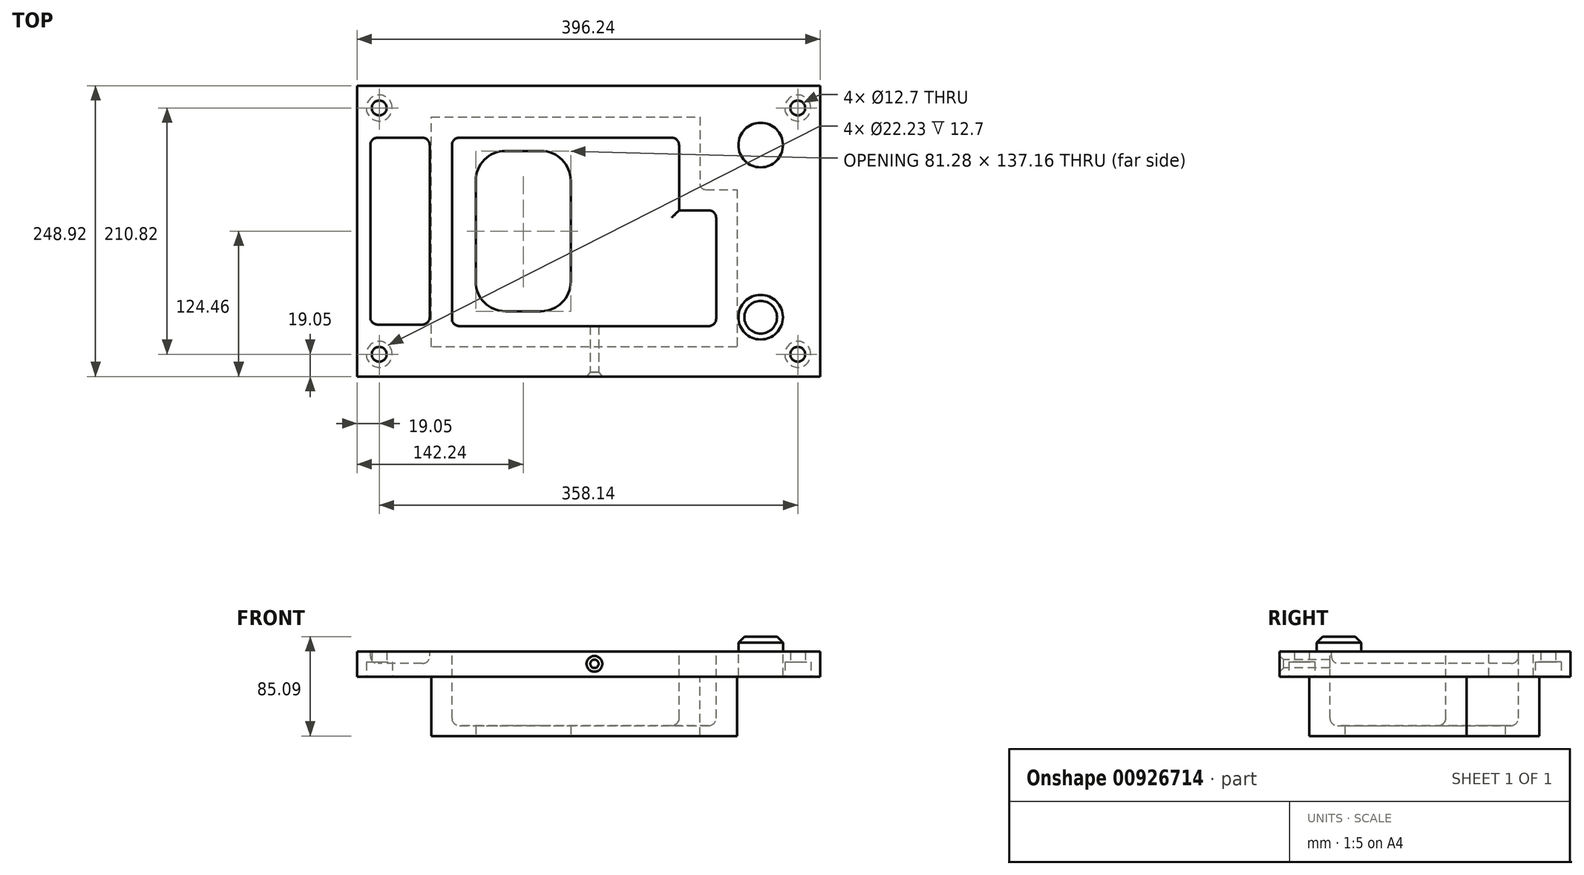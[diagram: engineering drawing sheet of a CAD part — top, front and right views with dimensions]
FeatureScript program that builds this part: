
annotation { "Feature Type Name" : "Feature", "Feature Type Description" : "" }
export const myFeature = defineFeature(function(context is Context, id is Id, definition is map)
    precondition{}
    {
        {
            var Q0;
            Q0=qCreatedBy(makeId("Top.planeOp"),FACE);
            var sketch = newSketch(context, id + "F0", { "sketchPlane" : qUnion([Q0])});
            skLineSegment(sketch, "E0.bottom", {"start": v(198.12, 124.46) * mm, "end": v(-198.12, 124.46) * mm});
            skLineSegment(sketch, "E0.top", {"start": v(198.12, -124.46) * mm, "end": v(-198.12, -124.46) * mm});
            skLineSegment(sketch, "E0.left", {"start": v(198.12, 124.46) * mm, "end": v(198.12, -124.46) * mm});
            skLineSegment(sketch, "E0.right", {"start": v(-198.12, 124.46) * mm, "end": v(-198.12, -124.46) * mm});
            skPoint(sketch, "E0.middle", {"position": v(0, 0) * mm});
            skSolve(sketch);
        }
        {
            var Q0;
            Q0=qSketchRegion(id+"F0",true);
            extrude(context, id + "F1", {"entities" : qUnion([Q0]), "oppositeDirection" : true, "depth" : 21.59 * mm, "offsetDistance" : 25.4 * mm});
        }
        {
            var Q0;
            Q0=makeQuery(id+"F1.opExtrude","CAP_FACE",FACE,{"disambiguationData":[OSD([sQuery(id+"F0.wireOp",EDGE,"E0.bottom"),sQuery(id+"F0.wireOp",EDGE,"E0.top"),sQuery(id+"F0.wireOp",EDGE,"E0.left"),sQuery(id+"F0.wireOp",EDGE,"E0.right")])],"isStart":false});
            var sketch = newSketch(context, id + "F2", { "sketchPlane" : qUnion([Q0])});
            skLineSegment(sketch, "E1", {"start": v(-134.62, 99.06) * mm, "end": v(-134.62, -97.79) * mm});
            skLineSegment(sketch, "E2", {"start": v(-134.62, -97.79) * mm, "end": v(95.25, -97.79) * mm});
            skLineSegment(sketch, "E3", {"start": v(95.25, -97.8) * mm, "end": v(95.25, -35.56) * mm});
            skLineSegment(sketch, "E4", {"start": v(95.25, -35.56) * mm, "end": v(127, -35.56) * mm});
            skLineSegment(sketch, "E5", {"start": v(127, -35.56) * mm, "end": v(127, 99.06) * mm});
            skLineSegment(sketch, "E6", {"start": v(127, 99.06) * mm, "end": v(-134.62, 99.06) * mm});
            skSolve(sketch);
        }
        {
            var Q0;
            Q0=qSketchRegion(id+"F2",true);
            extrude(context, id + "F3", {"entities" : qUnion([Q0]), "operationType" : NewBodyOperationType.ADD, "depth" : 50.8 * mm, "offsetDistance" : 25.4 * mm});
        }
        {
            var Q0;
            Q0=makeQuery(id+"F1.opExtrude","CAP_FACE",FACE,{"disambiguationData":[OSD([sQuery(id+"F0.wireOp",EDGE,"E0.bottom"),sQuery(id+"F0.wireOp",EDGE,"E0.top"),sQuery(id+"F0.wireOp",EDGE,"E0.left"),sQuery(id+"F0.wireOp",EDGE,"E0.right")])],"isStart":true});
            var sketch = newSketch(context, id + "F4", { "sketchPlane" : qUnion([Q0])});
            skLineSegment(sketch, "E7.0", {"start": v(127, -99.06) * mm, "end": v(-134.62, -99.06) * mm, "construction": true});
            skLineSegment(sketch, "E8.0", {"start": v(127, 35.56) * mm, "end": v(127, -99.06) * mm, "construction": true});
            skPoint(sketch, "E9.0", {"position": v(111.12, 35.56) * mm});
            skLineSegment(sketch, "E10.0", {"start": v(95.25, 97.8) * mm, "end": v(95.25, 35.56) * mm, "construction": true});
            skLineSegment(sketch, "E11.0", {"start": v(95.25, 35.56) * mm, "end": v(127, 35.56) * mm, "construction": true});
            skLineSegment(sketch, "E12.0", {"start": v(-134.62, 97.79) * mm, "end": v(95.25, 97.79) * mm, "construction": true});
            skLineSegment(sketch, "E13.0", {"start": v(-134.62, -99.06) * mm, "end": v(-134.62, 97.79) * mm, "construction": true});
            skLineSegment(sketch, "E14", {"start": v(109.22, -81.28) * mm, "end": v(109.22, 17.78) * mm});
            skLineSegment(sketch, "E15", {"start": v(109.22, 17.78) * mm, "end": v(77.47, 17.78) * mm});
            skLineSegment(sketch, "E16", {"start": v(77.47, 17.78) * mm, "end": v(77.47, 80) * mm});
            skLineSegment(sketch, "E17", {"start": v(77.47, 80) * mm, "end": v(-116.84, 80) * mm});
            skLineSegment(sketch, "E18", {"start": v(-116.84, 80) * mm, "end": v(-116.84, -81.28) * mm});
            skLineSegment(sketch, "E19", {"start": v(-116.84, -81.28) * mm, "end": v(109.22, -81.28) * mm});
            skSolve(sketch);
        }
        {
            var Q0;
            Q0=qSketchRegion(id+"F4",true);
            extrude(context, id + "F5", {"entities" : qUnion([Q0]), "operationType" : NewBodyOperationType.REMOVE, "oppositeDirection" : true, "depth" : 63.5 * mm, "offsetDistance" : 25.4 * mm});
        }
        {
            var Q0;
            Q0=makeQuery(id+"F5.boolean.opBoolean","COPY",FACE,{"derivedFrom":makeQuery(id+"F5.opExtrude","CAP_FACE",FACE,{"disambiguationData":[OSD([sQuery(id+"F4.wireOp",EDGE,"E14"),sQuery(id+"F4.wireOp",EDGE,"E15"),sQuery(id+"F4.wireOp",EDGE,"E16"),sQuery(id+"F4.wireOp",EDGE,"E17"),sQuery(id+"F4.wireOp",EDGE,"E18"),sQuery(id+"F4.wireOp",EDGE,"E19")])],"isStart":false})});
            var Q1;
            Q1=makeQuery(id+"F5.boolean.opBoolean","COPY",EDGE,{"derivedFrom":makeQuery(id+"F5.opExtrude","SWEPT_EDGE",EDGE,{"disambiguationData":[OSD([sQuery(id+"F4.wireOp",EDGE,"E14"),sQuery(id+"F4.wireOp",EDGE,"E19")])]})});
            var Q2;
            Q2=makeQuery(id+"F5.boolean.opBoolean","COPY",EDGE,{"derivedFrom":makeQuery(id+"F5.opExtrude","SWEPT_EDGE",EDGE,{"disambiguationData":[OSD([sQuery(id+"F4.wireOp",EDGE,"E18"),sQuery(id+"F4.wireOp",EDGE,"E19")])]})});
            var Q3;
            Q3=makeQuery(id+"F5.boolean.opBoolean","COPY",EDGE,{"derivedFrom":makeQuery(id+"F5.opExtrude","SWEPT_EDGE",EDGE,{"disambiguationData":[OSD([sQuery(id+"F4.wireOp",EDGE,"E17"),sQuery(id+"F4.wireOp",EDGE,"E18")])]})});
            var Q4;
            Q4=makeQuery(id+"F5.boolean.opBoolean","COPY",EDGE,{"derivedFrom":makeQuery(id+"F5.opExtrude","SWEPT_EDGE",EDGE,{"disambiguationData":[OSD([sQuery(id+"F4.wireOp",EDGE,"E14"),sQuery(id+"F4.wireOp",EDGE,"E15")])]})});
            var Q5;
            Q5=makeQuery(id+"F5.boolean.opBoolean","COPY",EDGE,{"derivedFrom":makeQuery(id+"F5.opExtrude","SWEPT_EDGE",EDGE,{"disambiguationData":[OSD([sQuery(id+"F4.wireOp",EDGE,"E16"),sQuery(id+"F4.wireOp",EDGE,"E17")])]})});
            fillet(context, id + "F6", {"entities" : qUnion([Q0, Q1, Q2, Q3, Q4, Q5]), "radius" : 6.35 * mm, "tangentPropagation" : true, "allowEdgeOverflow" : false});
        }
        {
            var Q0;
            Q0=makeQuery(id+"F3.opExtrude","SWEPT_EDGE",EDGE,{"disambiguationData":[OSD([sQuery(id+"F2.wireOp",EDGE,"E3"),sQuery(id+"F2.wireOp",EDGE,"E4")])]});
            fillet(context, id + "F7", {"entities" : qUnion([Q0]), "radius" : 5.08 * mm, "tangentPropagation" : true, "allowEdgeOverflow" : false});
        }
        {
            var Q0;
            Q0=makeQuery(id+"F3.opExtrude","CAP_FACE",FACE,{"disambiguationData":[OSD([sQuery(id+"F2.wireOp",EDGE,"E1"),sQuery(id+"F2.wireOp",EDGE,"E2"),sQuery(id+"F2.wireOp",EDGE,"E3"),sQuery(id+"F2.wireOp",EDGE,"E4"),sQuery(id+"F2.wireOp",EDGE,"E5"),sQuery(id+"F2.wireOp",EDGE,"E6")])],"isStart":false});
            var sketch = newSketch(context, id + "F8", { "sketchPlane" : qUnion([Q0])});
            skLineSegment(sketch, "E20.bottom", {"start": v(-96.52, -68.58) * mm, "end": v(-15.24, -68.58) * mm});
            skLineSegment(sketch, "E20.top", {"start": v(-96.52, 68.58) * mm, "end": v(-15.24, 68.58) * mm});
            skLineSegment(sketch, "E20.left", {"start": v(-96.52, -68.58) * mm, "end": v(-96.52, 68.58) * mm});
            skLineSegment(sketch, "E20.right", {"start": v(-15.24, -68.58) * mm, "end": v(-15.24, 68.58) * mm});
            skPoint(sketch, "E20.middle", {"position": v(-55.88, 0) * mm});
            skSolve(sketch);
        }
        {
            var Q0;
            Q0=qSketchRegion(id+"F8",true);
            extrude(context, id + "F9", {"entities" : qUnion([Q0]), "operationType" : NewBodyOperationType.REMOVE, "endBound" : BoundingType.THROUGH_ALL, "oppositeDirection" : true, "depth" : 25.4 * mm, "offsetDistance" : 25.4 * mm});
        }
        {
            var Q0;
            Q0=makeQuery(id+"F1.opExtrude","CAP_FACE",FACE,{"disambiguationData":[OSD([sQuery(id+"F0.wireOp",EDGE,"E0.bottom"),sQuery(id+"F0.wireOp",EDGE,"E0.top"),sQuery(id+"F0.wireOp",EDGE,"E0.left"),sQuery(id+"F0.wireOp",EDGE,"E0.right")])],"isStart":true});
            var sketch = newSketch(context, id + "F10", { "sketchPlane" : qUnion([Q0])});
            skLineSegment(sketch, "E21.bottom", {"start": v(-135.9, 80) * mm, "end": v(-186.7, 80) * mm});
            skLineSegment(sketch, "E21.top", {"start": v(-135.9, -80) * mm, "end": v(-186.7, -80) * mm});
            skLineSegment(sketch, "E21.left", {"start": v(-135.9, 80) * mm, "end": v(-135.9, -80) * mm});
            skLineSegment(sketch, "E21.right", {"start": v(-186.7, 80) * mm, "end": v(-186.7, -80) * mm});
            skPoint(sketch, "E21.middle", {"position": v(-161.3, 0) * mm});
            skSolve(sketch);
        }
        {
            var Q0;
            Q0=qSketchRegion(id+"F10",true);
            extrude(context, id + "F11", {"entities" : qUnion([Q0]), "operationType" : NewBodyOperationType.REMOVE, "oppositeDirection" : true, "depth" : 10.4 * mm, "offsetDistance" : 25.4 * mm});
        }
        {
            var Q0;
            Q0=makeQuery(id+"F11.boolean.opBoolean","COPY",FACE,{"derivedFrom":makeQuery(id+"F11.opExtrude","CAP_FACE",FACE,{"disambiguationData":[OSD([sQuery(id+"F10.wireOp",EDGE,"E21.bottom"),sQuery(id+"F10.wireOp",EDGE,"E21.top"),sQuery(id+"F10.wireOp",EDGE,"E21.left"),sQuery(id+"F10.wireOp",EDGE,"E21.right")])],"isStart":false})});
            var Q1;
            Q1=makeQuery(id+"F11.boolean.opBoolean","COPY",EDGE,{"derivedFrom":makeQuery(id+"F11.opExtrude","SWEPT_EDGE",EDGE,{"disambiguationData":[OSD([sQuery(id+"F10.wireOp",EDGE,"E21.bottom"),sQuery(id+"F10.wireOp",EDGE,"E21.right")])]})});
            var Q2;
            Q2=makeQuery(id+"F11.boolean.opBoolean","COPY",EDGE,{"derivedFrom":makeQuery(id+"F11.opExtrude","SWEPT_EDGE",EDGE,{"disambiguationData":[OSD([sQuery(id+"F10.wireOp",EDGE,"E21.bottom"),sQuery(id+"F10.wireOp",EDGE,"E21.left")])]})});
            var Q3;
            Q3=makeQuery(id+"F11.boolean.opBoolean","COPY",EDGE,{"derivedFrom":makeQuery(id+"F11.opExtrude","SWEPT_EDGE",EDGE,{"disambiguationData":[OSD([sQuery(id+"F10.wireOp",EDGE,"E21.top"),sQuery(id+"F10.wireOp",EDGE,"E21.left")])]})});
            var Q4;
            Q4=makeQuery(id+"F11.boolean.opBoolean","COPY",EDGE,{"derivedFrom":makeQuery(id+"F11.opExtrude","SWEPT_EDGE",EDGE,{"disambiguationData":[OSD([sQuery(id+"F10.wireOp",EDGE,"E21.top"),sQuery(id+"F10.wireOp",EDGE,"E21.right")])]})});
            fillet(context, id + "F12", {"entities" : qUnion([Q0, Q1, Q2, Q3, Q4]), "radius" : 6.35 * mm, "tangentPropagation" : true, "allowEdgeOverflow" : false});
        }
        {
            var Q0;
            Q0=makeQuery(id+"F1.opExtrude","CAP_FACE",FACE,{"disambiguationData":[OSD([sQuery(id+"F0.wireOp",EDGE,"E0.bottom"),sQuery(id+"F0.wireOp",EDGE,"E0.top"),sQuery(id+"F0.wireOp",EDGE,"E0.left"),sQuery(id+"F0.wireOp",EDGE,"E0.right")])],"isStart":true});
            var sketch = newSketch(context, id + "F13", { "sketchPlane" : qUnion([Q0])});
            skLineSegment(sketch, "E22.bottom", {"start": v(160.02, 86.36) * mm, "end": v(134.62, 86.36) * mm});
            skLineSegment(sketch, "E22.top", {"start": v(160.02, 60.96) * mm, "end": v(134.62, 60.96) * mm});
            skLineSegment(sketch, "E22.left", {"start": v(160.02, 86.36) * mm, "end": v(160.02, 60.96) * mm});
            skLineSegment(sketch, "E22.right", {"start": v(134.62, 86.36) * mm, "end": v(134.62, 60.96) * mm});
            skPoint(sketch, "E22.middle", {"position": v(147.32, 73.66) * mm});
            skCircle(sketch, "E23", {"center": v(147.32, -73.66) * mm, "radius": 19.05 * mm});
            skSolve(sketch);
        }
        {
            var Q0;
            Q0=makeQuery(id+"F13.imprint","IMPRINT",FACE,{"disambiguationData":[TD([[makeQuery(id+"F13.imprint","IMPRINT",EDGE,{"derivedFrom":sQuery(id+"F13.wireOp",EDGE,"E23")}),1.0]])]});
            extrude(context, id + "F14", {"entities" : qUnion([Q0]), "operationType" : NewBodyOperationType.ADD, "depth" : 12.7 * mm, "offsetDistance" : 25.4 * mm});
        }
        {
            var Q0;
            Q0=makeQuery(id+"F14.opExtrude","CAP_FACE",FACE,{"disambiguationData":[OSD([sQuery(id+"F13.wireOp",EDGE,"E22.bottom"),sQuery(id+"F13.wireOp",EDGE,"E22.top"),sQuery(id+"F13.wireOp",EDGE,"E22.left"),sQuery(id+"F13.wireOp",EDGE,"E22.right")])],"isStart":false});
            var Q1;
            Q1=makeQuery(id+"F14.opExtrude","CAP_FACE",FACE,{"disambiguationData":[OSD([sQuery(id+"F13.wireOp",EDGE,"E23")])],"isStart":false});
            chamfer(context, id + "F15", {"entities" : qUnion([Q0, Q1]), "width" : 5.08 * mm, "tangentPropagation" : true});
        }
        {
            var Q0;
            Q0=makeQuery(id+"F1.opExtrude","SWEPT_FACE",FACE,{"disambiguationData":[OSD([sQuery(id+"F0.wireOp",EDGE,"E0.top")])]});
            var sketch = newSketch(context, id + "F16", { "sketchPlane" : qUnion([Q0])});
            skPoint(sketch, "E24", {"position": v(5.08, -10.67) * mm});
            skSolve(sketch);
        }
        {
            var Q0;
            Q0=sQuery(id+"F16.wireOp",VERTEX,"E24");
            var Q1;
            Q1=makeQuery(id+"F1.opExtrude","SWEPT_BODY",BODY,{"disambiguationData":[OSD([sQuery(id+"F0.wireOp",EDGE,"E0.bottom"),sQuery(id+"F0.wireOp",EDGE,"E0.top"),sQuery(id+"F0.wireOp",EDGE,"E0.left"),sQuery(id+"F0.wireOp",EDGE,"E0.right")])]});
            hole(context, id + "F17", {"style" : HoleStyle.C_SINK, "endStyle" : HoleEndStyle.BLIND, "standardTappedOrClearance" : lookupTablePath({ "fit" : "Normal (ASME)", "standard" : "ANSI", "size" : "1/4", "type" : "Clearance" }), "standardBlindInLast" : lookupTablePath({ "fit" : "Normal", "standard" : "ANSI", "size" : "1/4", "type" : "Clearance" }), "holeDiameter" : 7.14 * mm, "cSinkDiameter" : 13.5 * mm, "cSinkAngle" : 82 * degree, "majorDiameter" : 6.35 * mm, "holeDepth" : 127 * mm, "isTappedThrough" : true, "tappedDepth" : 12.7 * mm, "tapClearance" : 3, "locations" : qUnion([Q0]), "scope" : qUnion([Q1])});
        }
        {
            var Q0;
            Q0=makeQuery(id+"F2.imprint","IMPRINT",FACE,{"disambiguationData":[TD([[makeQuery(id+"F2.imprint","IMPRINT",EDGE,{"derivedFrom":sQuery(id+"F2.wireOp",EDGE,"E1")}),-1.0]])]});
            var sketch = newSketch(context, id + "F18", { "sketchPlane" : qUnion([Q0])});
            skLineSegment(sketch, "E25.bottom", {"start": v(179.07, -105.41) * mm, "end": v(-179.07, -105.41) * mm});
            skLineSegment(sketch, "E25.top", {"start": v(179.07, 105.41) * mm, "end": v(-179.07, 105.41) * mm});
            skLineSegment(sketch, "E25.left", {"start": v(179.07, -105.41) * mm, "end": v(179.07, 105.41) * mm});
            skLineSegment(sketch, "E25.right", {"start": v(-179.07, -105.41) * mm, "end": v(-179.07, 105.41) * mm});
            skPoint(sketch, "E25.middle", {"position": v(0, 0) * mm});
            skSolve(sketch);
        }
        {
            var Q0;
            Q0=sQuery(id+"F18.wireOp",VERTEX,"E25.top.end");
            var Q1;
            Q1=sQuery(id+"F18.wireOp",VERTEX,"E25.top.start");
            var Q2;
            Q2=sQuery(id+"F18.wireOp",VERTEX,"E25.bottom.start");
            var Q3;
            Q3=sQuery(id+"F18.wireOp",VERTEX,"E25.bottom.end");
            var Q4;
            Q4=makeQuery(id+"F1.opExtrude","SWEPT_BODY",BODY,{"disambiguationData":[OSD([sQuery(id+"F0.wireOp",EDGE,"E0.bottom"),sQuery(id+"F0.wireOp",EDGE,"E0.top"),sQuery(id+"F0.wireOp",EDGE,"E0.left"),sQuery(id+"F0.wireOp",EDGE,"E0.right")])]});
            hole(context, id + "F19", {"style" : HoleStyle.C_BORE, "endStyle" : HoleEndStyle.THROUGH, "holeDiameter" : 12.7 * mm, "cBoreDiameter" : 22.22 * mm, "cBoreDepth" : 12.7 * mm, "majorDiameter" : 6.35 * mm, "isTappedThrough" : true, "tappedDepth" : 12.7 * mm, "tapClearance" : 3, "locations" : qUnion([Q0, Q1, Q2, Q3]), "scope" : qUnion([Q4])});
        }
        {
            var Q0;
            Q0=makeQuery(id+"F1.opExtrude","CAP_FACE",FACE,{"disambiguationData":[OSD([sQuery(id+"F0.wireOp",EDGE,"E0.bottom"),sQuery(id+"F0.wireOp",EDGE,"E0.top"),sQuery(id+"F0.wireOp",EDGE,"E0.left"),sQuery(id+"F0.wireOp",EDGE,"E0.right")])],"isStart":true});
            var sketch = newSketch(context, id + "F20", { "sketchPlane" : qUnion([Q0])});
            skCircle(sketch, "E26", {"center": v(147.32, 73.66) * mm, "radius": 19.05 * mm});
            skSolve(sketch);
        }
        {
            var Q0;
            Q0=qSketchRegion(id+"F20",true);
            extrude(context, id + "F21", {"entities" : qUnion([Q0]), "operationType" : NewBodyOperationType.REMOVE, "endBound" : BoundingType.THROUGH_ALL, "oppositeDirection" : true, "depth" : 25.4 * mm, "offsetDistance" : 25.4 * mm});
        }
        {
            var Q0;
            Q0=makeQuery(id+"F9.boolean.opBoolean","COPY",EDGE,{"derivedFrom":makeQuery(id+"F9.opExtrude","SWEPT_EDGE",EDGE,{"disambiguationData":[OSD([sQuery(id+"F8.wireOp",EDGE,"E20.top"),sQuery(id+"F8.wireOp",EDGE,"E20.right")])]})});
            var Q1;
            Q1=makeQuery(id+"F9.boolean.opBoolean","COPY",EDGE,{"derivedFrom":makeQuery(id+"F9.opExtrude","SWEPT_EDGE",EDGE,{"disambiguationData":[OSD([sQuery(id+"F8.wireOp",EDGE,"E20.bottom"),sQuery(id+"F8.wireOp",EDGE,"E20.right")])]})});
            var Q2;
            Q2=makeQuery(id+"F9.boolean.opBoolean","COPY",EDGE,{"derivedFrom":makeQuery(id+"F9.opExtrude","SWEPT_EDGE",EDGE,{"disambiguationData":[OSD([sQuery(id+"F8.wireOp",EDGE,"E20.bottom"),sQuery(id+"F8.wireOp",EDGE,"E20.left")])]})});
            var Q3;
            Q3=makeQuery(id+"F9.boolean.opBoolean","COPY",EDGE,{"derivedFrom":makeQuery(id+"F9.opExtrude","SWEPT_EDGE",EDGE,{"disambiguationData":[OSD([sQuery(id+"F8.wireOp",EDGE,"E20.top"),sQuery(id+"F8.wireOp",EDGE,"E20.left")])]})});
            fillet(context, id + "F22", {"entities" : qUnion([Q0, Q1, Q2, Q3]), "radius" : 25.4 * mm, "tangentPropagation" : true, "allowEdgeOverflow" : false});
        }
    });
